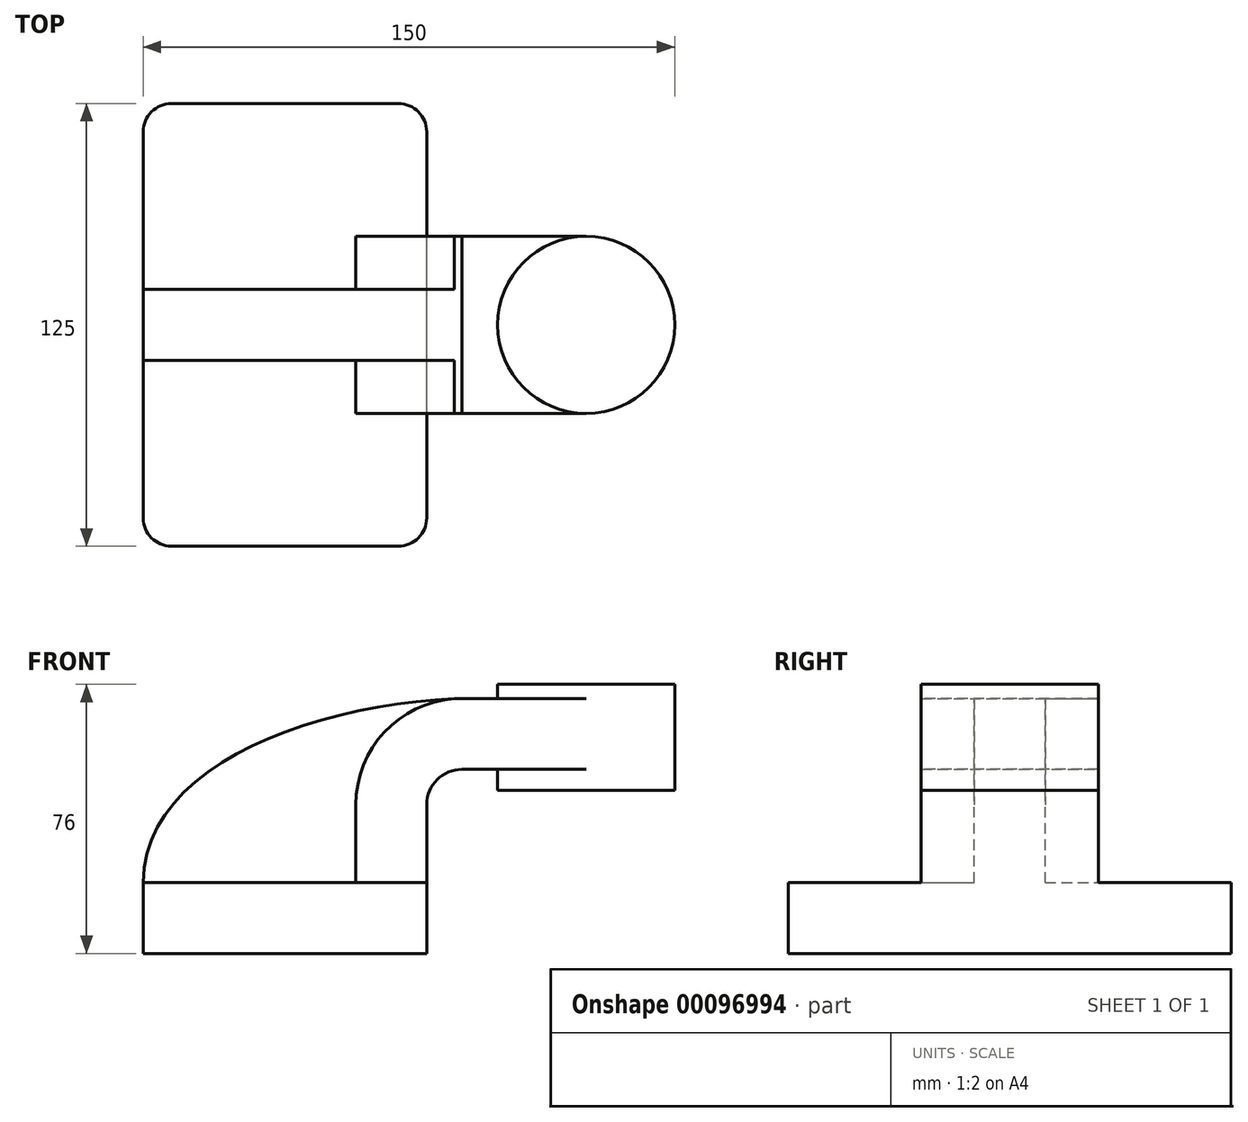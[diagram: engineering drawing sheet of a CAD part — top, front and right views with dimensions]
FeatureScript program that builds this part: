
annotation { "Feature Type Name" : "Feature", "Feature Type Description" : "" }
export const myFeature = defineFeature(function(context is Context, id is Id, definition is map)
    precondition{}
    {
        {
            var Q0;
            Q0=qCreatedBy(makeId("Front.planeOp"),FACE);
            var sketch = newSketch(context, id + "F0", { "sketchPlane" : qUnion([Q0])});
            skLineSegment(sketch, "E0.bottom", {"start": v(-40, 10) * mm, "end": v(40, 10) * mm});
            skLineSegment(sketch, "E0.top", {"start": v(-40, -10) * mm, "end": v(40, -10) * mm});
            skLineSegment(sketch, "E0.left", {"start": v(-40, 10) * mm, "end": v(-40, -10) * mm});
            skLineSegment(sketch, "E0.right", {"start": v(40, 10) * mm, "end": v(40, -10) * mm});
            skPoint(sketch, "E0.middle", {"position": v(0, 0) * mm});
            skLineSegment(sketch, "E1.bottom", {"start": v(110, 36) * mm, "end": v(60, 36) * mm});
            skLineSegment(sketch, "E1.top", {"start": v(110, 66) * mm, "end": v(60, 66) * mm});
            skLineSegment(sketch, "E1.left", {"start": v(110, 36) * mm, "end": v(110, 66) * mm});
            skLineSegment(sketch, "E1.right", {"start": v(60, 36) * mm, "end": v(60, 66) * mm});
            skPoint(sketch, "E1.middle", {"position": v(85, 51) * mm});
            skLineSegment(sketch, "E2", {"start": v(40, 10) * mm, "end": v(40, 32) * mm});
            skArc(sketch, "E3", {"start": v(40, 32) * mm, "mid": v(42.93, 39.07) * mm, "end": v(50, 42) * mm});
            skLineSegment(sketch, "E4", {"start": v(50, 42) * mm, "end": v(85, 42) * mm});
            skLineSegment(sketch, "E5.0", {"start": v(50, 62) * mm, "end": v(85, 62) * mm});
            skArc(sketch, "E5.1", {"start": v(20, 32) * mm, "mid": v(28.79, 53.21) * mm, "end": v(50, 62) * mm});
            skLineSegment(sketch, "E5.2", {"start": v(20, 10) * mm, "end": v(20, 32) * mm});
            skLineSegment(sketch, "E6", {"start": v(85, 66) * mm, "end": v(85, 36) * mm});
            skFitSpline(sketch, "E7", {"points": [v(-40, 10) * mm, v(50, 62) * mm], "startDerivative": vector(0, 99.06) * mm, "endDerivative": vector(124.62, 3.65) * mm});
            skSolve(sketch);
        }
        {
            var Q0;
            Q0=makeQuery(id+"F0.imprint","IMPRINT",FACE,{"disambiguationData":[TD([[makeQuery(id+"F0.imprint","IMPRINT",EDGE,{"derivedFrom":sQuery(id+"F0.wireOp",EDGE,"E0.top")}),1.0]])]});
            extrude(context, id + "F1", {"entities" : qUnion([Q0]), "endBound" : BoundingType.SYMMETRIC, "depth" : 125 * mm});
        }
        {
            var Q0;
            {var subQ1=sQuery(id+"F0.wireOp",EDGE,"E2");Q0=makeQuery(id+"F0.imprint","IMPRINT",FACE,{"disambiguationData":[TD([[makeQuery(id+"F0.imprint","IMPRINT",EDGE,{"derivedFrom":subQ1}),1.0]])]});}
            var Q1;
            {var subQ0=sQuery(id+"F0.wireOp",EDGE,"E4");var subQ1=sQuery(id+"F0.wireOp",EDGE,"E1.right");var subQ2=makeQuery(id+"F0.imprint","INTERSECT",VERTEX,{"derivedFrom":[subQ1,subQ0]});Q1=makeQuery(id+"F0.imprint","IMPRINT",FACE,{"disambiguationData":[TD([[makeQuery(id+"F0.imprint","IMPRINT",EDGE,{"disambiguationData":[TD([[subQ2,-1.0]])],"derivedFrom":subQ1}),-1.0]])]});}
            extrude(context, id + "F2", {"entities" : qUnion([Q0, Q1]), "operationType" : NewBodyOperationType.ADD, "endBound" : BoundingType.SYMMETRIC, "depth" : 50 * mm});
        }
        {
            var Q0;
            {var subQ3=sQuery(id+"F0.wireOp",EDGE,"E5.2");Q0=makeQuery(id+"F0.imprint","IMPRINT",FACE,{"disambiguationData":[TD([[makeQuery(id+"F0.imprint","IMPRINT",EDGE,{"derivedFrom":subQ3}),1.0]])]});}
            extrude(context, id + "F3", {"entities" : qUnion([Q0]), "operationType" : NewBodyOperationType.ADD, "endBound" : BoundingType.SYMMETRIC, "depth" : 20 * mm});
        }
        {
            var Q0;
            {var subQ0=sQuery(id+"F0.wireOp",EDGE,"E1.left");Q0=makeQuery(id+"F0.imprint","IMPRINT",FACE,{"disambiguationData":[TD([[makeQuery(id+"F0.imprint","IMPRINT",EDGE,{"derivedFrom":subQ0}),1.0]])]});}
            var Q1;
            Q1=sQuery(id+"F0.wireOp",EDGE,"E6");
            revolve(context, id + "F4", {"operationType" : NewBodyOperationType.ADD, "entities" : qUnion([Q0]), "axis" : qUnion([Q1]), "revolveType" : RevolveType.FULL});
        }
        {
            var Q0;
            Q0=makeQuery(id+"F1.opExtrude","CAP_EDGE",EDGE,{"disambiguationData":[OSD([sQuery(id+"F0.wireOp",EDGE,"E0.right")])],"isStart":false});
            var Q1;
            Q1=makeQuery(id+"F1.opExtrude","CAP_EDGE",EDGE,{"disambiguationData":[OSD([sQuery(id+"F0.wireOp",EDGE,"E0.right")])],"isStart":true});
            var Q2;
            Q2=makeQuery(id+"F1.opExtrude","CAP_EDGE",EDGE,{"disambiguationData":[OSD([sQuery(id+"F0.wireOp",EDGE,"E0.left")])],"isStart":false});
            var Q3;
            Q3=makeQuery(id+"F1.opExtrude","CAP_EDGE",EDGE,{"disambiguationData":[OSD([sQuery(id+"F0.wireOp",EDGE,"E0.left")])],"isStart":true});
            fillet(context, id + "F5", {"entities" : qUnion([Q0, Q1, Q2, Q3]), "radius" : 8 * mm, "tangentPropagation" : true, "allowEdgeOverflow" : false});
        }
    });
